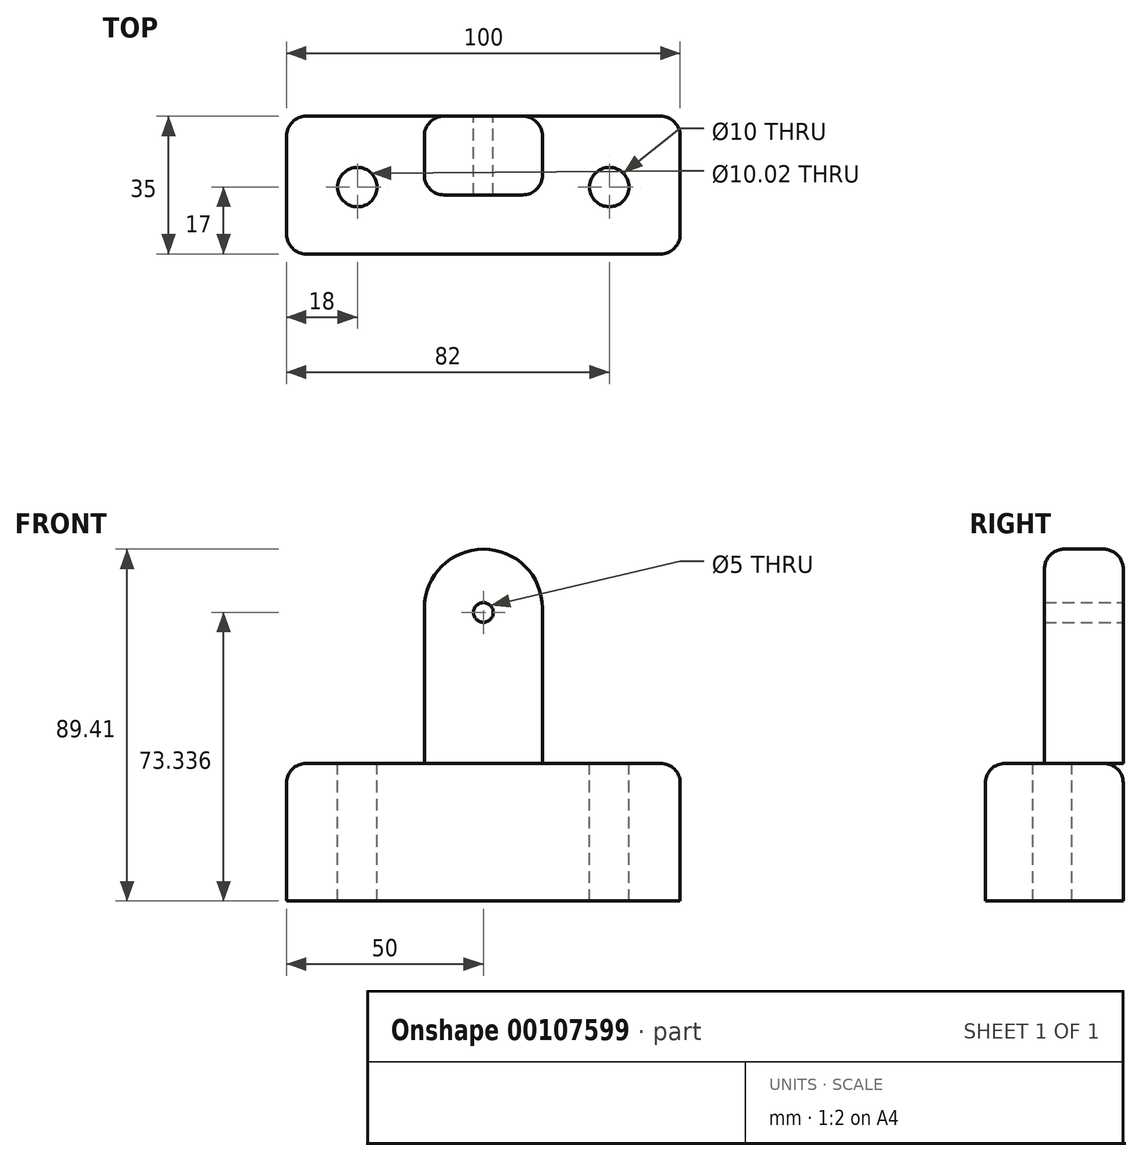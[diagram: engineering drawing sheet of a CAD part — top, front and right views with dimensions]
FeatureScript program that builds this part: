
annotation { "Feature Type Name" : "Feature", "Feature Type Description" : "" }
export const myFeature = defineFeature(function(context is Context, id is Id, definition is map)
    precondition{}
    {
        {
            var Q0;
            Q0=qCreatedBy(makeId("Front.planeOp"),FACE);
            var sketch = newSketch(context, id + "F0", { "sketchPlane" : qUnion([Q0])});
            skLineSegment(sketch, "E0.bottom", {"start": v(-50, -7.83) * mm, "end": v(50, -7.83) * mm});
            skLineSegment(sketch, "E0.top", {"start": v(-50, -42.83) * mm, "end": v(50, -42.83) * mm});
            skLineSegment(sketch, "E0.left", {"start": v(-50, -7.83) * mm, "end": v(-50, -42.83) * mm});
            skLineSegment(sketch, "E0.right", {"start": v(50, -7.83) * mm, "end": v(50, -42.83) * mm});
            skPoint(sketch, "E0.middle", {"position": v(0, -25.33) * mm});
            skSolve(sketch);
        }
        {
            var Q0;
            Q0=makeQuery(id+"F0.imprint","IMPRINT",FACE,{"disambiguationData":[TD([[makeQuery(id+"F0.imprint","IMPRINT",EDGE,{"derivedFrom":sQuery(id+"F0.wireOp",EDGE,"E0.bottom")}),-1.0]])]});
            extrude(context, id + "F1", {"entities" : qUnion([Q0]), "depth" : 35 * mm});
        }
        {
            var Q0;
            Q0=qCreatedBy(makeId("Front.planeOp"),FACE);
            var sketch = newSketch(context, id + "F2", { "sketchPlane" : qUnion([Q0])});
            skLineSegment(sketch, "E1.bottom", {"start": v(-15, -7.83) * mm, "end": v(15, -7.83) * mm});
            skLineSegment(sketch, "E1.top", {"start": v(-15, 31.58) * mm, "end": v(15, 31.58) * mm});
            skLineSegment(sketch, "E1.left", {"start": v(-15, -7.83) * mm, "end": v(-15, 31.58) * mm});
            skLineSegment(sketch, "E1.right", {"start": v(15, -7.83) * mm, "end": v(15, 31.58) * mm});
            skArc(sketch, "E2", {"start": v(-15, 31.58) * mm, "mid": v(0, 46.58) * mm, "end": v(15, 31.58) * mm});
            skSolve(sketch);
        }
        {
            var Q0;
            Q0=makeQuery(id+"F2.imprint","IMPRINT",FACE,{"disambiguationData":[TD([[makeQuery(id+"F2.imprint","IMPRINT",EDGE,{"derivedFrom":sQuery(id+"F2.wireOp",EDGE,"E1.bottom")}),1.0]])]});
            var Q1;
            Q1=makeQuery(id+"F2.imprint","IMPRINT",FACE,{"disambiguationData":[TD([[makeQuery(id+"F2.imprint","IMPRINT",EDGE,{"derivedFrom":sQuery(id+"F2.wireOp",EDGE,"E1.top")}),1.0]])]});
            extrude(context, id + "F3", {"entities" : qUnion([Q0, Q1]), "depth" : 20 * mm});
        }
        {
            var Q0;
            Q0=makeQuery(id+"F3.opExtrude","CAP_EDGE",EDGE,{"disambiguationData":[OSD([sQuery(id+"F2.wireOp",EDGE,"E2")])],"isStart":true});
            var Q1;
            Q1=makeQuery(id+"F3.opExtrude","CAP_EDGE",EDGE,{"disambiguationData":[OSD([sQuery(id+"F2.wireOp",EDGE,"E2")])],"isStart":false});
            var Q2;
            Q2=makeQuery(id+"F1.opExtrude","SWEPT_EDGE",EDGE,{"disambiguationData":[OSD([sQuery(id+"F0.wireOp",EDGE,"E0.bottom"),sQuery(id+"F0.wireOp",EDGE,"E0.left")])]});
            var Q3;
            Q3=makeQuery(id+"F1.opExtrude","CAP_EDGE",EDGE,{"disambiguationData":[OSD([sQuery(id+"F0.wireOp",EDGE,"E0.left")])],"isStart":true});
            var Q4;
            Q4=makeQuery(id+"F1.opExtrude","CAP_EDGE",EDGE,{"disambiguationData":[OSD([sQuery(id+"F0.wireOp",EDGE,"E0.left")])],"isStart":false});
            var Q5;
            Q5=makeQuery(id+"F1.opExtrude","CAP_EDGE",EDGE,{"disambiguationData":[OSD([sQuery(id+"F0.wireOp",EDGE,"E0.bottom")])],"isStart":true});
            var Q6;
            Q6=makeQuery(id+"F1.opExtrude","CAP_EDGE",EDGE,{"disambiguationData":[OSD([sQuery(id+"F0.wireOp",EDGE,"E0.bottom")])],"isStart":false});
            var Q7;
            Q7=makeQuery(id+"F1.opExtrude","SWEPT_EDGE",EDGE,{"disambiguationData":[OSD([sQuery(id+"F0.wireOp",EDGE,"E0.bottom"),sQuery(id+"F0.wireOp",EDGE,"E0.right")])]});
            var Q8;
            Q8=makeQuery(id+"F1.opExtrude","CAP_EDGE",EDGE,{"disambiguationData":[OSD([sQuery(id+"F0.wireOp",EDGE,"E0.right")])],"isStart":false});
            var Q9;
            Q9=makeQuery(id+"F1.opExtrude","CAP_EDGE",EDGE,{"disambiguationData":[OSD([sQuery(id+"F0.wireOp",EDGE,"E0.right")])],"isStart":true});
            fillet(context, id + "F4", {"entities" : qUnion([Q0, Q1, Q2, Q3, Q4, Q5, Q6, Q7, Q8, Q9]), "radius" : 5 * mm, "tangentPropagation" : true, "allowEdgeOverflow" : false});
        }
        {
            var Q0;
            Q0=qCreatedBy(makeId("Top.planeOp"),FACE);
            var sketch = newSketch(context, id + "F5", { "sketchPlane" : qUnion([Q0])});
            skCircle(sketch, "E3", {"center": v(32, -18) * mm, "radius": 5 * mm});
            skCircle(sketch, "E4", {"center": v(-32, -18) * mm, "radius": 5 * mm});
            skSolve(sketch);
        }
        {
            var Q0;
            Q0=makeQuery(id+"F5.imprint","IMPRINT",FACE,{"disambiguationData":[TD([[makeQuery(id+"F5.imprint","IMPRINT",EDGE,{"derivedFrom":sQuery(id+"F5.wireOp",EDGE,"E4")}),1.0]])]});
            var Q1;
            Q1=makeQuery(id+"F5.imprint","IMPRINT",FACE,{"disambiguationData":[TD([[makeQuery(id+"F5.imprint","IMPRINT",EDGE,{"derivedFrom":sQuery(id+"F5.wireOp",EDGE,"E3")}),1.0]])]});
            extrude(context, id + "F6", {"entities" : qUnion([Q0, Q1]), "operationType" : NewBodyOperationType.REMOVE, "oppositeDirection" : true, "depth" : 50 * mm});
        }
        {
            var Q0;
            Q0=qCreatedBy(makeId("Front.planeOp"),FACE);
            var sketch = newSketch(context, id + "F7", { "sketchPlane" : qUnion([Q0])});
            skCircle(sketch, "E5", {"center": v(0, 30.5) * mm, "radius": 2.5 * mm});
            skSolve(sketch);
        }
        {
            var Q0;
            Q0=makeQuery(id+"F7.imprint","IMPRINT",FACE,{"disambiguationData":[TD([[makeQuery(id+"F7.imprint","IMPRINT",EDGE,{"derivedFrom":sQuery(id+"F7.wireOp",EDGE,"E5")}),1.0]])]});
            extrude(context, id + "F8", {"entities" : qUnion([Q0]), "operationType" : NewBodyOperationType.REMOVE, "depth" : 30 * mm});
        }
    });
